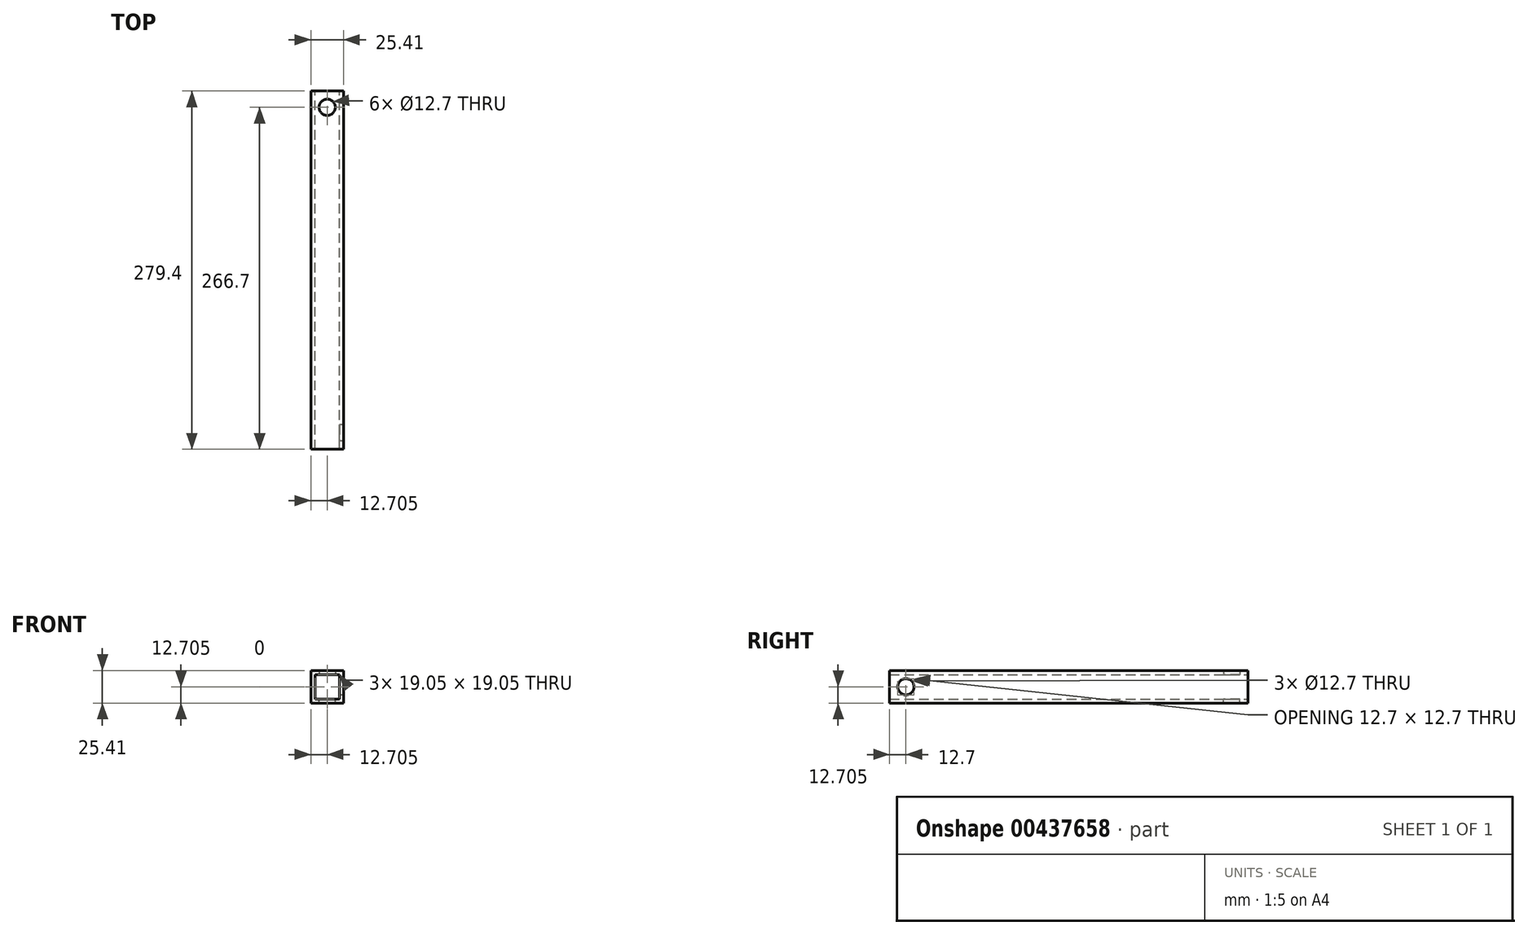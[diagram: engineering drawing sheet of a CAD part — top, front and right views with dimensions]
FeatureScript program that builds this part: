
annotation { "Feature Type Name" : "Feature", "Feature Type Description" : "" }
export const myFeature = defineFeature(function(context is Context, id is Id, definition is map)
    precondition{}
    {
        {
            var Q0;
            Q0=qCreatedBy(makeId("Front.planeOp"),FACE);
            var sketch = newSketch(context, id + "F0", { "sketchPlane" : qUnion([Q0])});
            skLineSegment(sketch, "E0.bottom", {"start": v(-22.23, 22.23) * mm, "end": v(3.17, 22.23) * mm});
            skLineSegment(sketch, "E0.top", {"start": v(-22.23, -3.18) * mm, "end": v(3.18, -3.18) * mm});
            skLineSegment(sketch, "E0.left", {"start": v(-22.23, 22.23) * mm, "end": v(-22.23, -3.18) * mm});
            skLineSegment(sketch, "E0.right", {"start": v(3.17, 22.23) * mm, "end": v(3.18, -3.18) * mm});
            skLineSegment(sketch, "E1.bottom", {"start": v(-19.05, 19.05) * mm, "end": v(0, 19.05) * mm});
            skLineSegment(sketch, "E1.top", {"start": v(-19.05, 0) * mm, "end": v(0, 0) * mm});
            skLineSegment(sketch, "E1.left", {"start": v(-19.05, 19.05) * mm, "end": v(-19.05, 0) * mm});
            skLineSegment(sketch, "E1.right", {"start": v(0, 19.05) * mm, "end": v(0, 0) * mm});
            skSolve(sketch);
        }
        {
            var Q0;
            Q0=qSketchRegion(id+"F0",true);
            extrude(context, id + "F1", {"entities" : qUnion([Q0]), "depth" : 279.4 * mm, "offsetDistance" : 25.4 * mm});
        }
        {
            var Q0;
            Q0=qCreatedBy(makeId("Top.planeOp"),FACE);
            var sketch = newSketch(context, id + "F2", { "sketchPlane" : qUnion([Q0])});
            skPoint(sketch, "E2", {"position": v(-9.53, -12.7) * mm});
            skSolve(sketch);
        }
        {
            var Q0;
            Q0=sQuery(id+"F2.wireOp",VERTEX,"E2");
            var Q1;
            Q1=makeQuery(id+"F1.opExtrude","SWEPT_BODY",BODY,{"disambiguationData":[OSD([sQuery(id+"F0.wireOp",EDGE,"E0.bottom"),sQuery(id+"F0.wireOp",EDGE,"E0.top"),sQuery(id+"F0.wireOp",EDGE,"E0.left"),sQuery(id+"F0.wireOp",EDGE,"E0.right"),sQuery(id+"F0.wireOp",EDGE,"E1.bottom"),sQuery(id+"F0.wireOp",EDGE,"E1.top"),sQuery(id+"F0.wireOp",EDGE,"E1.left"),sQuery(id+"F0.wireOp",EDGE,"E1.right")])]});
            hole(context, id + "F3", {"style" : HoleStyle.SIMPLE, "endStyle" : HoleEndStyle.THROUGH, "holeDiameter" : 12.7 * mm, "isTappedThrough" : true, "tappedDepth" : 12.7 * mm, "tapClearance" : 3, "locations" : qUnion([Q0]), "scope" : qUnion([Q1])});
        }
        {
            var Q0;
            Q0=qCreatedBy(makeId("Top.planeOp"),FACE);
            var sketch = newSketch(context, id + "F4", { "sketchPlane" : qUnion([Q0])});
            skPoint(sketch, "E3", {"position": v(-9.53, -12.7) * mm});
            skSolve(sketch);
        }
        {
            var Q0;
            Q0=sQuery(id+"F4.wireOp",VERTEX,"E3");
            var Q1;
            Q1=makeQuery(id+"F1.opExtrude","SWEPT_BODY",BODY,{"disambiguationData":[OSD([sQuery(id+"F0.wireOp",EDGE,"E0.bottom"),sQuery(id+"F0.wireOp",EDGE,"E0.top"),sQuery(id+"F0.wireOp",EDGE,"E0.left"),sQuery(id+"F0.wireOp",EDGE,"E0.right"),sQuery(id+"F0.wireOp",EDGE,"E1.bottom"),sQuery(id+"F0.wireOp",EDGE,"E1.top"),sQuery(id+"F0.wireOp",EDGE,"E1.left"),sQuery(id+"F0.wireOp",EDGE,"E1.right")])]});
            hole(context, id + "F5", {"style" : HoleStyle.SIMPLE, "endStyle" : HoleEndStyle.THROUGH, "oppositeDirection" : true, "holeDiameter" : 12.7 * mm, "isTappedThrough" : true, "tappedDepth" : 12.7 * mm, "tapClearance" : 3, "locations" : qUnion([Q0]), "scope" : qUnion([Q1])});
        }
        {
            var Q0;
            Q0=qCreatedBy(makeId("Right.planeOp"),FACE);
            var sketch = newSketch(context, id + "F6", { "sketchPlane" : qUnion([Q0])});
            skPoint(sketch, "E4", {"position": v(-266.7, 9.52) * mm});
            skSolve(sketch);
        }
        {
            var Q0;
            Q0=sQuery(id+"F6.wireOp",VERTEX,"E4");
            var Q1;
            Q1=makeQuery(id+"F1.opExtrude","SWEPT_BODY",BODY,{"disambiguationData":[OSD([sQuery(id+"F0.wireOp",EDGE,"E0.bottom"),sQuery(id+"F0.wireOp",EDGE,"E0.top"),sQuery(id+"F0.wireOp",EDGE,"E0.left"),sQuery(id+"F0.wireOp",EDGE,"E0.right"),sQuery(id+"F0.wireOp",EDGE,"E1.bottom"),sQuery(id+"F0.wireOp",EDGE,"E1.top"),sQuery(id+"F0.wireOp",EDGE,"E1.left"),sQuery(id+"F0.wireOp",EDGE,"E1.right")])]});
            hole(context, id + "F7", {"style" : HoleStyle.SIMPLE, "endStyle" : HoleEndStyle.THROUGH, "oppositeDirection" : true, "holeDiameter" : 12.7 * mm, "isTappedThrough" : true, "tappedDepth" : 12.7 * mm, "tapClearance" : 3, "locations" : qUnion([Q0]), "scope" : qUnion([Q1])});
        }
    });
